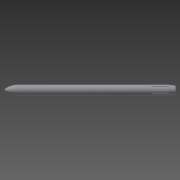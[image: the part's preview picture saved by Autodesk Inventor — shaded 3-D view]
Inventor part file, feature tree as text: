
AUTODESK INVENTOR PART (.ipt)
format: ipt  version: 2014 SP1 (Build 180222100, 222)  size: 271,360 bytes
history: native  units: mm
features: plane x8, sketch x8, extrude x4, pattern_circular x2, revolve x2, shell x1, fillet x1, projected_geometry x1
ambient origin geometry x8: Origin, YZ Plane, XZ Plane, XY Plane, X Axis, Y Axis, Z Axis, Center Point
bodies: Solid1 (feature_tree)
feature tree (27):
  extrude  "Extrusion1"  Depth=1200.0mm TaperAngle=0.0deg
  plane  "Work Plane1"
  plane  "Work Plane2"
  extrude  "Extrusion4"  Depth=5.0mm
  pattern_circular  "Circular Pattern2"  Count=2 Angle=360.0deg
  sketch  "Sketch5"  dims[d28=25.0mm d29=0.0mm d30=20.0mm d31=360.0deg]
  plane  "Work Plane3"
  plane  "Work Plane4"
  extrude  "Extrusion5"  Depth=35.0mm
  pattern_circular  "Circular Pattern3"  Count=11  [1 undecoded]
  plane  "Work Plane5"
  extrude  "Extrusion6"  Depth=10.0mm TaperAngle=360.0deg
  plane  "Work Plane6"
  revolve  "Revolution2"  [1 undecoded]
  plane  "Work Plane7"
  revolve  "Revolution3"  [1 undecoded]
  shell  "Shell1"  Thickness=450.0mm
  fillet  "Fillet2"  [1 undecoded]
  plane  "Work Plane8"
  sketch  "Sketch11"  dims[d53=5.0mm d54=10.0mm d55=0.0mm d62=450.0mm d63=0.0mm d67=90.0deg d68=0.0mm d69=28.0mm d70=90.0deg d72=3.0mm d73=1.5mm d74=0.0mm]
  sketch  "Sketch1"  dims[d0=70.0mm d1=1200.0mm d2=0.0mm]
  sketch  "Sketch4"  dims[d10=35.0mm d21=35.0mm d26=5.0mm]
  sketch  "Sketch7"  dims[d33=0.0mm d39=35.0mm]
  sketch  "Sketch8"  dims[d41=5.0mm d42=110.0mm]
  sketch  "Sketch9"  dims[d43=10.0mm d44=0.0mm d45=80.0mm d46=360.0deg]
  sketch  "Sketch10"  dims[d49=-35.0mm d52=36.0mm]
  projected_geometry  "Projected Loop1"
note: 4 required parameter values undecoded (feature->parameter linkage not recoverable at this tier; creation-order binding heuristic only, values carry confidence <= 0.55)